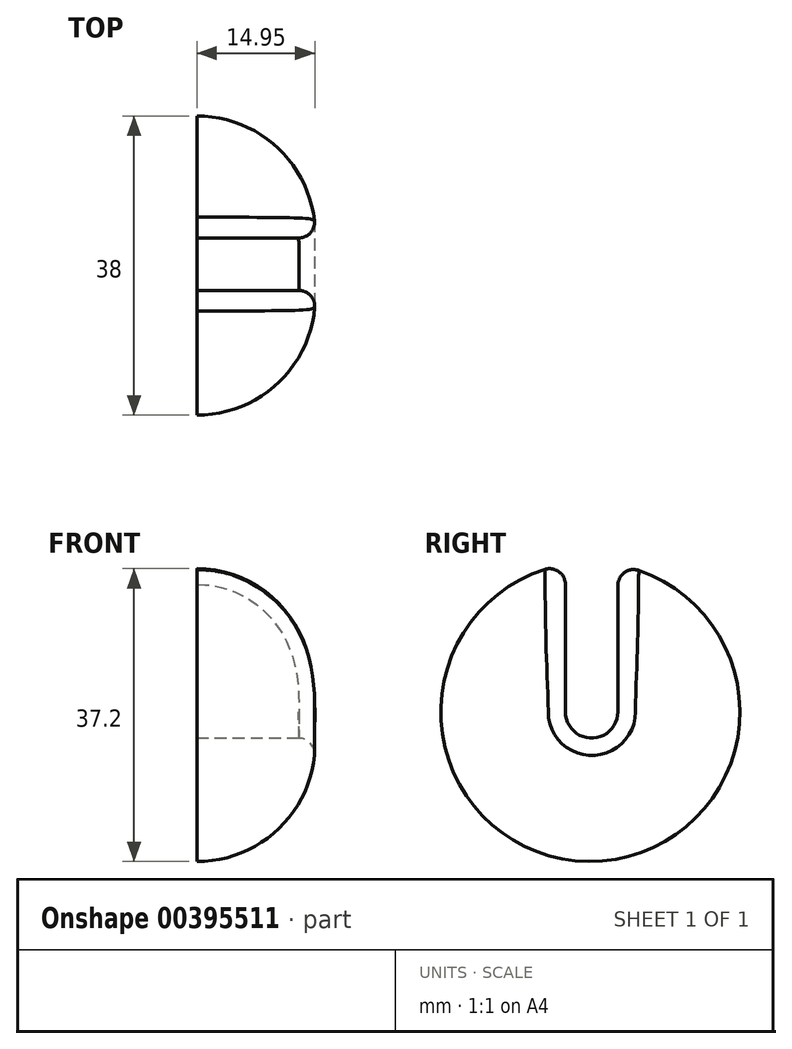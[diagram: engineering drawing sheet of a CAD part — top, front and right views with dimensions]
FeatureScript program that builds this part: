
annotation { "Feature Type Name" : "Feature", "Feature Type Description" : "" }
export const myFeature = defineFeature(function(context is Context, id is Id, definition is map)
    precondition{}
    {
        {
            var Q0;
            Q0=qCreatedBy(makeId("Right.planeOp"),FACE);
            var sketch = newSketch(context, id + "F0", { "sketchPlane" : qUnion([Q0])});
            skCircle(sketch, "E0", {"center": v(0, 0) * mm, "radius": 19 * mm});
            skLineSegment(sketch, "E1.bottom", {"start": v(3.5, 22.37) * mm, "end": v(-3.17, 22.37) * mm});
            skLineSegment(sketch, "E1.left", {"start": v(3.5, 22.37) * mm, "end": v(3.5, 0) * mm});
            skLineSegment(sketch, "E1.right", {"start": v(-3.17, 22.37) * mm, "end": v(-3.17, 0) * mm});
            skArc(sketch, "E2", {"start": v(-3.17, 0) * mm, "mid": v(0.17, -3.33) * mm, "end": v(3.5, 0) * mm});
            skPoint(sketch, "E3", {"position": v(-12.53, 0) * mm});
            skPoint(sketch, "E4", {"position": v(12.87, 0) * mm});
            skPoint(sketch, "E5", {"position": v(0, -13.82) * mm});
            skSolve(sketch);
        }
        {
            var Q0;
            {var subQ5=sQuery(id+"F0.wireOp",EDGE,"E2");Q0=makeQuery(id+"F0.imprint","IMPRINT",FACE,{"disambiguationData":[TD([[makeQuery(id+"F0.imprint","IMPRINT",EDGE,{"derivedFrom":subQ5}),-1.0]])]});}
            var Q1;
            {var subQ5=sQuery(id+"F0.wireOp",EDGE,"E2");Q1=makeQuery(id+"F0.imprint","IMPRINT",FACE,{"disambiguationData":[TD([[makeQuery(id+"F0.imprint","IMPRINT",EDGE,{"derivedFrom":subQ5}),1.0]])]});}
            extrude(context, id + "F1", {"entities" : qUnion([Q0, Q1]), "depth" : 15 * mm});
        }
        {
            var Q0;
            {var subQ5=sQuery(id+"F0.wireOp",EDGE,"E1.bottom");Q0=makeQuery(id+"F0.imprint","IMPRINT",FACE,{"disambiguationData":[TD([[makeQuery(id+"F0.imprint","IMPRINT",EDGE,{"derivedFrom":subQ5}),1.0]])]});}
            var Q1;
            {var subQ5=sQuery(id+"F0.wireOp",EDGE,"E2");Q1=makeQuery(id+"F0.imprint","IMPRINT",FACE,{"disambiguationData":[TD([[makeQuery(id+"F0.imprint","IMPRINT",EDGE,{"derivedFrom":subQ5}),1.0]])]});}
            extrude(context, id + "F2", {"entities" : qUnion([Q0, Q1]), "operationType" : NewBodyOperationType.REMOVE, "depth" : 17.9 * mm});
        }
        {
            var Q0;
            Q0=makeQuery(id+"F1.opExtrude","CAP_EDGE",EDGE,{"disambiguationData":[OSD([sQuery(id+"F0.wireOp",EDGE,"E0")])],"isStart":false});
            fillet(context, id + "F3", {"entities" : qUnion([Q0]), "radius" : 15 * mm, "tangentPropagation" : true, "allowEdgeOverflow" : false});
        }
        {
            var Q0;
            Q0=makeQuery(id+"F2.boolean.opBoolean","INTERSECT",EDGE,{"derivedFrom":[makeQuery(id+"F1.opExtrude","CAP_FACE",FACE,{"disambiguationData":[OSD([sQuery(id+"F0.wireOp",EDGE,"E0")])],"isStart":false}),makeQuery(id+"F2.opExtrude","SWEPT_FACE",FACE,{"disambiguationData":[OSD([sQuery(id+"F0.wireOp",EDGE,"E2")])]})]});
            fillet(context, id + "F4", {"entities" : qUnion([Q0]), "radius" : 2 * mm, "tangentPropagation" : true, "allowEdgeOverflow" : false});
        }
        {
            var Q0;
            Q0=sQuery(id+"F0.wireOp",VERTEX,"E3");
            var Q1;
            Q1=sQuery(id+"F0.wireOp",VERTEX,"E5");
            var Q2;
            Q2=sQuery(id+"F0.wireOp",VERTEX,"E4");
            var Q3;
            Q3=makeQuery(id+"F1.opExtrude","SWEPT_BODY",BODY,{"disambiguationData":[OSD([sQuery(id+"F0.wireOp",EDGE,"E0")])]});
            hole(context, id + "F5", {"style" : HoleStyle.C_BORE, "endStyle" : HoleEndStyle.THROUGH, "standardTappedOrClearance" : lookupTablePath({ "standard" : "ISO", "size" : "5", "type" : "Drilled" }), "standardBlindInLast" : lookupTablePath({ "standard" : "ISO", "size" : "5", "type" : "Drilled" }), "holeDiameter" : 5 * mm, "cBoreDiameter" : 6.5 * mm, "cBoreDepth" : 3 * mm, "isTappedThrough" : true, "tappedDepth" : 12 * mm, "tapClearance" : 3, "locations" : qUnion([Q0, Q1, Q2]), "scope" : qUnion([Q3])});
        }
    });
